# Revit family: GEM1
name_source: partatom
category: Lighting Fixtures
revit_build: Autodesk Revit 2013 (Build: 20130531_2115(x64)
units: mm (PartAtom-declared; Revit-internal decimal feet)

## types (1)
- GEM1_Performance_Bollard
    Apparent Load = 0 VA
    Assembly Code = D5020200
    Color Filter = 16777215
    Default Elevation = 0"
    Description = Architectural Outdoor Lighting
    Dimming Lamp Color Temperature Shift = <None>
    Emit Shape Visible in Rendering = No
    Emit from Circle Diameter = 6"
    Finish = All colors shall be a Super TGIC thermoset polyester powder coat paint
    Full Load Current = 0 A
    Glass Material = Glass-Kim Lighting-Clear
    Housing material = Metal-Kim Lighting-Aluminum Alloy
    Lamp = LED
    Load Classification = Lighting
    Manufacturer = KIM Lighting
    Manufacturer Fax = 626-369-2695
    MasterFormat Title = Parking Lighting, Roadway Lighting, Site Lighting
    Model = GEM1
    Note Text = LF
    Note Visible = Yes
    Number of Poles = 1
    OmniClass Number = 23.80.70.14.11.11
    OmniClass Title = Lighting Bollard
    Overall Height = 42 1/2"
    Photometric Notes = More IES files download on Photometric Web Link
    Photometric Web File = gem1-18l3k.ies
    Photometric Web Link = http://www.kimlighting.com
    Power Factor = 1
    Product Documentation Link = http://www.kimlighting.com
    Product Page URL = http://www.kimlighting.com
    Revision Date = 01/11/17
    Series = Low Level LED Bollard
    Shaft Height = 33"
    Shaft Material = Metal-Kim Lighting-Aluminum Alloy
    Tilt Angle = 90.00°
    Type Comments = Lighting Fixture
    URL = www.kimlighting.com/
    Voltage = 120 V
    Wattage Comments = 21W to 41W

## geometry (parser evidence)
native form markers: Blend x10, Sweep x3
no freeform markers — native parametric forms only
